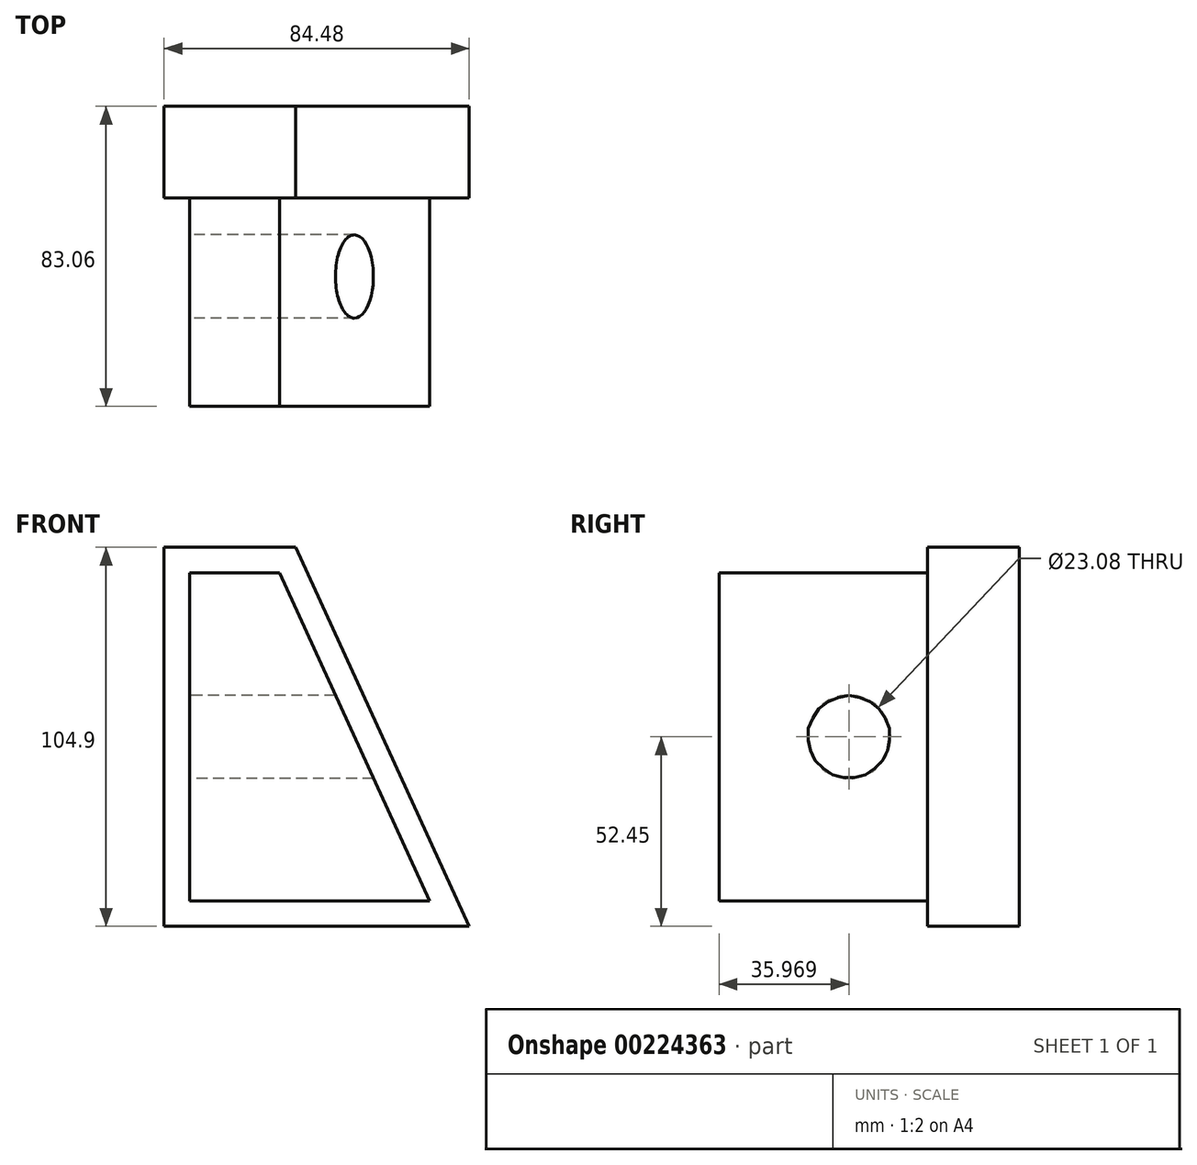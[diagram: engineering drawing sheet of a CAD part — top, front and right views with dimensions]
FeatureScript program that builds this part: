
annotation { "Feature Type Name" : "Feature", "Feature Type Description" : "" }
export const myFeature = defineFeature(function(context is Context, id is Id, definition is map)
    precondition{}
    {
        {
            var Q0;
            Q0=qCreatedBy(makeId("Front.planeOp"),FACE);
            var sketch = newSketch(context, id + "F0", { "sketchPlane" : qUnion([Q0])});
            skLineSegment(sketch, "E0.bottom", {"start": v(-5.78, 52.45) * mm, "end": v(-42.24, 52.45) * mm});
            skLineSegment(sketch, "E0.top", {"start": v(42.24, -52.45) * mm, "end": v(-42.24, -52.45) * mm});
            skLineSegment(sketch, "E0.right", {"start": v(-42.24, 52.45) * mm, "end": v(-42.24, -52.45) * mm});
            skPoint(sketch, "E0.middle", {"position": v(0, 0) * mm});
            skLineSegment(sketch, "E1", {"start": v(86.26, -19.73) * mm, "end": v(91.6, -22.1) * mm});
            skLineSegment(sketch, "E2", {"start": v(-5.78, 52.45) * mm, "end": v(42.24, -52.45) * mm});
            skPoint(sketch, "E0.left.start.orphan", {"position": v(42.24, 52.45) * mm});
            skSolve(sketch);
        }
        {
            var Q0;
            Q0=makeQuery(id+"F0.imprint","IMPRINT",FACE,{"disambiguationData":[TD([[makeQuery(id+"F0.imprint","IMPRINT",EDGE,{"derivedFrom":sQuery(id+"F0.wireOp",EDGE,"E0.bottom")}),1.0]])]});
            extrude(context, id + "F1", {"entities" : qUnion([Q0]), "depth" : 25.4 * mm});
        }
        {
            var Q0;
            Q0=makeQuery(id+"F1.opExtrude","CAP_FACE",FACE,{"disambiguationData":[OSD([sQuery(id+"F0.wireOp",EDGE,"E0.bottom"),sQuery(id+"F0.wireOp",EDGE,"E0.top"),sQuery(id+"F0.wireOp",EDGE,"E0.right"),sQuery(id+"F0.wireOp",EDGE,"E2")])],"isStart":false});
            var sketch = newSketch(context, id + "F2", { "sketchPlane" : qUnion([Q0])});
            skLineSegment(sketch, "E3.0", {"start": v(-35.19, -45.4) * mm, "end": v(31.26, -45.4) * mm});
            skLineSegment(sketch, "E3.1", {"start": v(-35.19, 45.4) * mm, "end": v(-35.19, -56.14) * mm});
            skLineSegment(sketch, "E3.2", {"start": v(-10.3, 45.4) * mm, "end": v(-35.19, 45.4) * mm});
            skLineSegment(sketch, "E3.3", {"start": v(35.75, -55.2) * mm, "end": v(-10.3, 45.4) * mm});
            skSolve(sketch);
        }
        {
            var Q0;
            {var subQ0=sQuery(id+"F2.wireOp",EDGE,"E3.0");Q0=makeQuery(id+"F2.imprint","IMPRINT",FACE,{"disambiguationData":[TD([[makeQuery(id+"F2.imprint","IMPRINT",EDGE,{"derivedFrom":subQ0}),1.0]])]});}
            extrude(context, id + "F3", {"entities" : qUnion([Q0]), "operationType" : NewBodyOperationType.ADD, "depth" : 57.66 * mm});
        }
        {
            var Q0;
            Q0=makeQuery(id+"F3.opExtrude","SWEPT_FACE",FACE,{"disambiguationData":[OSD([sQuery(id+"F2.wireOp",EDGE,"E3.1")])]});
            var sketch = newSketch(context, id + "F4", { "sketchPlane" : qUnion([Q0])});
            skCircle(sketch, "E4", {"center": v(47.1, 0) * mm, "radius": 11.54 * mm});
            skSolve(sketch);
        }
        {
            var Q0;
            Q0=makeQuery(id+"F4.imprint","IMPRINT",FACE,{"disambiguationData":[TD([[makeQuery(id+"F4.imprint","IMPRINT",EDGE,{"derivedFrom":sQuery(id+"F4.wireOp",EDGE,"E4")}),1.0]])]});
            extrude(context, id + "F5", {"entities" : qUnion([Q0]), "operationType" : NewBodyOperationType.REMOVE, "oppositeDirection" : true, "depth" : 726.2 * mm});
        }
    });
